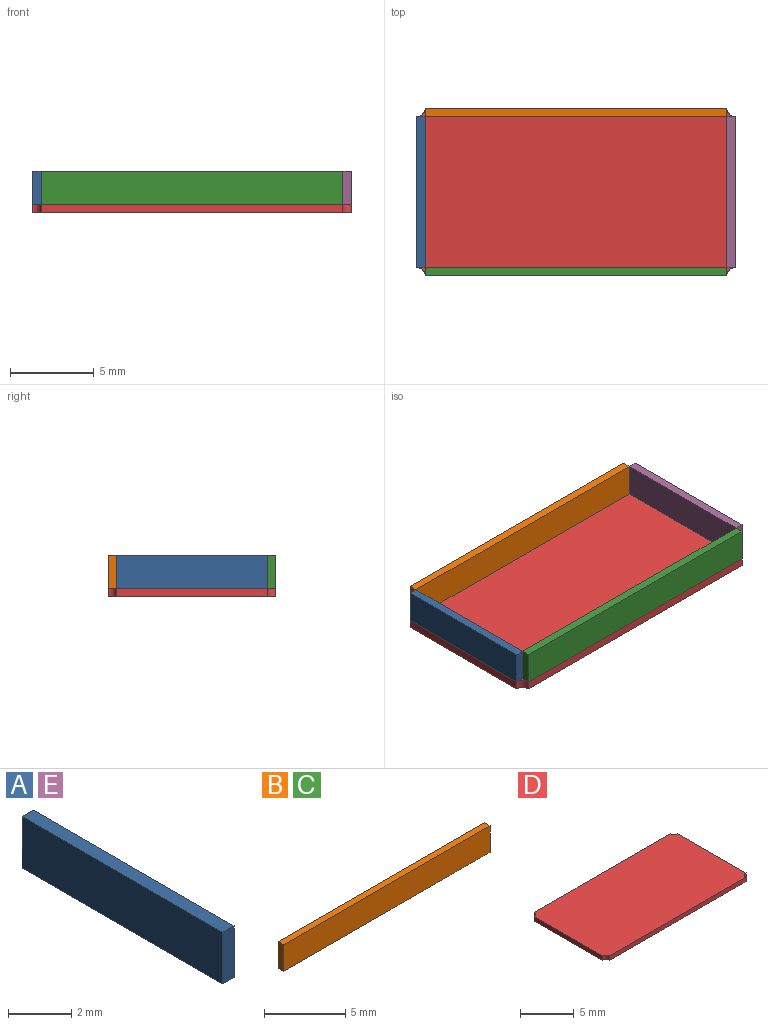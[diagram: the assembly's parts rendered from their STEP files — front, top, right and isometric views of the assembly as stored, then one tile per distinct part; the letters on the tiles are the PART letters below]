
ASSEMBLY  parts=5 mates=4
PART A: 6 faces, bbox 0.5x9x2 mm
  f0: plane 2x0.5mm, normal (0,1,0), area 1mm2, adj f1,f3,f4,f5
  f1: plane 9x0.5mm, normal (0,0,1), area 4.5mm2, adj f0,f2,f4,f5
  f2: plane 2x0.5mm, normal (0,-1,0), area 1mm2, adj f1,f3,f4,f5
  f3: plane 9x0.5mm, normal (0,0,-1), area 4.5mm2, adj f0,f2,f4,f5
  f4: plane 9x2mm, normal (1,0,0), area 18mm2, adj f0,f1,f2,f3
  f5: plane 9x2mm, normal (-1,0,0), area 18mm2, adj f0,f1,f2,f3
PART B: 6 faces, bbox 18x0.5x2 mm
  f0: plane 2x0.5mm, normal (1,0,0), area 1mm2, adj f1,f3,f4,f5
  f1: plane 18x0.5mm, normal (0,0,1), area 9mm2, adj f0,f2,f4,f5
  f2: plane 2x0.5mm, normal (-1,0,0), area 1mm2, adj f1,f3,f4,f5
  f3: plane 18x0.5mm, normal (0,0,-1), area 9mm2, adj f0,f2,f4,f5
  f4: plane 18x2mm, normal (0,-1,0), area 36mm2, adj f0,f1,f2,f3
  f5: plane 18x2mm, normal (0,1,0), area 36mm2, adj f0,f1,f2,f3
PART C: same geometry as B
PART D: 10 faces, bbox 19x10x0.5 mm
  f0: cylinder r=0.5mm len=0.5mm, axis (0,0,-1), area 0.4mm2, adj f1,f7,f8,f9
  f1: plane 18x0.5mm, normal (0,1,0), area 9mm2, adj f0,f2,f8,f9
  f2: cylinder r=0.5mm len=0.5mm, axis (0,0,-1), area 0.4mm2, adj f1,f3,f8,f9
  f3: plane 9x0.5mm, normal (-1,0,0), area 4.5mm2, adj f2,f4,f8,f9
  f4: cylinder r=0.5mm len=0.5mm, axis (0,0,-1), area 0.4mm2, adj f3,f5,f8,f9
  f5: plane 18x0.5mm, normal (0,-1,0), area 9mm2, adj f4,f6,f8,f9
  f6: cylinder r=0.5mm len=0.5mm, axis (0,0,-1), area 0.4mm2, adj f5,f7,f8,f9
  f7: plane 9x0.5mm, normal (1,0,0), area 4.5mm2, adj f0,f6,f8,f9
  f8: plane 19x10mm, normal (0,0,1), area 189.2mm2, adj f0,f1,f2,f3,f4,f5,f6,f7
  f9: plane 19x10mm, normal (0,0,-1), area 189.2mm2, adj f0,f1,f2,f3,f4,f5,f6,f7
PART E: same geometry as A
PLACE A t=(-3.55,3.12,5.29)mm
PLACE B t=(5.95,8.12,5.29)mm
PLACE C t=(5.95,-1.38,5.29)mm
PLACE D t=(5.95,3.12,3.79)mm fixed
PLACE E t=(14.95,3.12,5.29)mm
MATE fastened A.f3 <-> D.f8  axis (0,0,-1) through (-3.3,3.12,4.29)mm
MATE fastened B.f3 <-> D.f8  axis (0,0,-1) through (5.95,7.87,4.29)mm
MATE fastened C.f3 <-> D.f8  axis (0,0,-1) through (5.95,-1.63,4.29)mm
MATE fastened E.f3 <-> D.f8  axis (0,0,-1) through (15.2,3.12,4.29)mm
